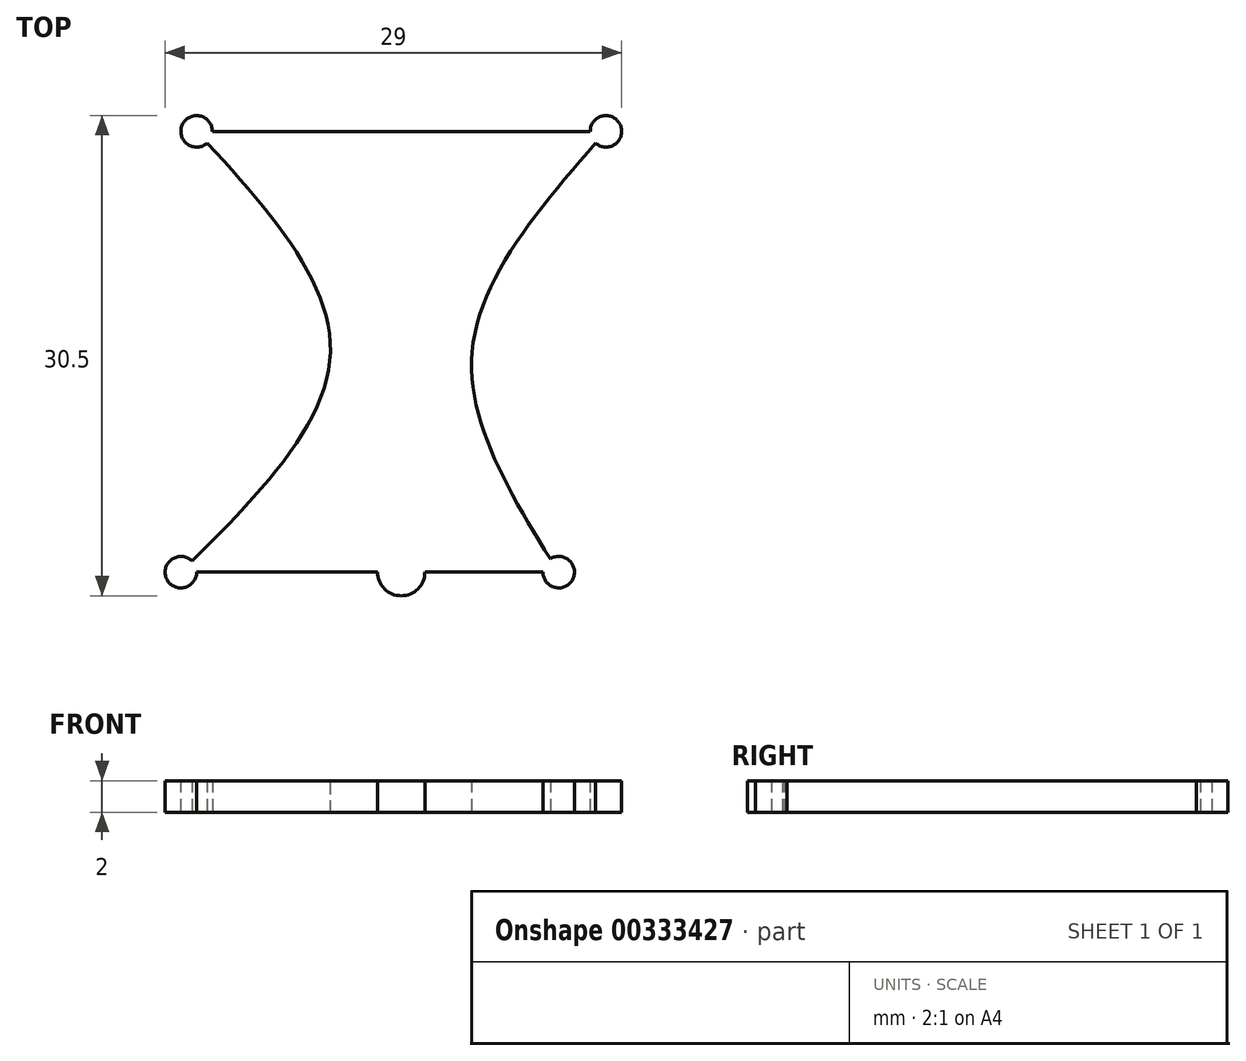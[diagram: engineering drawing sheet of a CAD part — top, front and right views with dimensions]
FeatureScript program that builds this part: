
annotation { "Feature Type Name" : "Feature", "Feature Type Description" : "" }
export const myFeature = defineFeature(function(context is Context, id is Id, definition is map)
    precondition{}
    {
        {
            var Q0;
            Q0=qCreatedBy(makeId("Top.planeOp"),FACE);
            var sketch = newSketch(context, id + "F0", { "sketchPlane" : qUnion([Q0])});
            skLineSegment(sketch, "E0", {"start": v(-13, 0) * mm, "end": v(13, 0) * mm});
            skArc(sketch, "E1", {"start": v(-1.5, 0) * mm, "mid": v(0, 1.5) * mm, "end": v(1.5, 0) * mm});
            skLineSegment(sketch, "E2", {"start": v(0, 0) * mm, "end": v(0, -28) * mm});
            skLineSegment(sketch, "E3", {"start": v(-14, -28) * mm, "end": v(10, -28) * mm});
            skPoint(sketch, "E4", {"position": v(0, -14) * mm});
            skLineSegment(sketch, "E5", {"start": v(-4.5, -14) * mm, "end": v(4.5, -14) * mm});
            skFitSpline(sketch, "E6", {"points": [v(-14, -28) * mm, v(-4.5, -14) * mm, v(-13, 0) * mm], "startDerivative": vector(27.92, 27.66) * mm, "endDerivative": vector(-26.06, 28.34) * mm});
            skFitSpline(sketch, "E7", {"points": [v(10, -28) * mm, v(4.5, -14) * mm, v(13, 0) * mm], "startDerivative": vector(-18.06, 28.9) * mm, "endDerivative": vector(23.77, 27.11) * mm});
            skCircle(sketch, "E8", {"center": v(13, 0) * mm, "radius": 1 * mm});
            skCircle(sketch, "E9", {"center": v(-13, 0) * mm, "radius": 1 * mm});
            skCircle(sketch, "E10", {"center": v(-14, -28) * mm, "radius": 1 * mm});
            skCircle(sketch, "E11", {"center": v(10, -28) * mm, "radius": 1 * mm});
            skArc(sketch, "E12", {"start": v(-1.5, -28) * mm, "mid": v(0, -29.5) * mm, "end": v(1.5, -28) * mm});
            skSolve(sketch);
        }
        {
            var Q0;
            {var subQ5=sQuery(id+"F0.wireOp",EDGE,"E0");var subQ7=makeQuery(id+"F0.imprint","INTERSECT",VERTEX,{"disambiguationData":[OD(0.0)],"derivedFrom":[subQ5,sQuery(id+"F0.wireOp",EDGE,"E1")]});Q0=makeQuery(id+"F0.imprint","IMPRINT",FACE,{"disambiguationData":[TD([[makeQuery(id+"F0.imprint","IMPRINT",EDGE,{"disambiguationData":[TD([[subQ7,1.0]])],"derivedFrom":subQ5}),-1.0]])]});}
            var Q1;
            {var subQ0=sQuery(id+"F0.wireOp",EDGE,"E6");var subQ1=sQuery(id+"F0.wireOp",EDGE,"E0");var subQ2=makeQuery(id+"F0.imprint","INTERSECT",VERTEX,{"derivedFrom":[subQ1,subQ0]});Q1=makeQuery(id+"F0.imprint","IMPRINT",FACE,{"disambiguationData":[TD([[makeQuery(id+"F0.imprint","IMPRINT",EDGE,{"disambiguationData":[TD([[subQ2,-1.0]])],"derivedFrom":subQ1}),1.0]])]});}
            var Q2;
            {var subQ0=sQuery(id+"F0.wireOp",EDGE,"E6");var subQ1=sQuery(id+"F0.wireOp",EDGE,"E0");var subQ2=makeQuery(id+"F0.imprint","INTERSECT",VERTEX,{"derivedFrom":[subQ1,subQ0]});Q2=makeQuery(id+"F0.imprint","IMPRINT",FACE,{"disambiguationData":[TD([[makeQuery(id+"F0.imprint","IMPRINT",EDGE,{"disambiguationData":[TD([[subQ2,-1.0]])],"derivedFrom":subQ1}),-1.0]])]});}
            var Q3;
            {var subQ0=sQuery(id+"F0.wireOp",EDGE,"E1");Q3=makeQuery(id+"F0.imprint","IMPRINT",FACE,{"disambiguationData":[TD([[makeQuery(id+"F0.imprint","IMPRINT",EDGE,{"derivedFrom":subQ0}),-1.0]])]});}
            var Q4;
            {var subQ5=sQuery(id+"F0.wireOp",EDGE,"E0");var subQ7=makeQuery(id+"F0.imprint","INTERSECT",VERTEX,{"disambiguationData":[OD(1.0)],"derivedFrom":[subQ5,sQuery(id+"F0.wireOp",EDGE,"E1")]});Q4=makeQuery(id+"F0.imprint","IMPRINT",FACE,{"disambiguationData":[TD([[makeQuery(id+"F0.imprint","IMPRINT",EDGE,{"disambiguationData":[TD([[subQ7,1.0]])],"derivedFrom":subQ5}),-1.0]])]});}
            var Q5;
            {var subQ0=sQuery(id+"F0.wireOp",EDGE,"E7");var subQ1=sQuery(id+"F0.wireOp",EDGE,"E0");var subQ2=makeQuery(id+"F0.imprint","INTERSECT",VERTEX,{"derivedFrom":[subQ1,subQ0]});Q5=makeQuery(id+"F0.imprint","IMPRINT",FACE,{"disambiguationData":[TD([[makeQuery(id+"F0.imprint","IMPRINT",EDGE,{"disambiguationData":[TD([[subQ2,1.0]])],"derivedFrom":subQ1}),-1.0]])]});}
            var Q6;
            {var subQ0=sQuery(id+"F0.wireOp",EDGE,"E7");var subQ1=sQuery(id+"F0.wireOp",EDGE,"E0");var subQ2=makeQuery(id+"F0.imprint","INTERSECT",VERTEX,{"derivedFrom":[subQ1,subQ0]});Q6=makeQuery(id+"F0.imprint","IMPRINT",FACE,{"disambiguationData":[TD([[makeQuery(id+"F0.imprint","IMPRINT",EDGE,{"disambiguationData":[TD([[subQ2,1.0]])],"derivedFrom":subQ1}),1.0]])]});}
            var Q7;
            {var subQ0=sQuery(id+"F0.wireOp",EDGE,"E7");var subQ1=sQuery(id+"F0.wireOp",EDGE,"E3");var subQ2=makeQuery(id+"F0.imprint","INTERSECT",VERTEX,{"derivedFrom":[subQ1,subQ0]});Q7=makeQuery(id+"F0.imprint","IMPRINT",FACE,{"disambiguationData":[TD([[makeQuery(id+"F0.imprint","IMPRINT",EDGE,{"disambiguationData":[TD([[subQ2,1.0]])],"derivedFrom":subQ1}),-1.0]])]});}
            var Q8;
            {var subQ0=sQuery(id+"F0.wireOp",EDGE,"E7");var subQ1=sQuery(id+"F0.wireOp",EDGE,"E3");var subQ2=makeQuery(id+"F0.imprint","INTERSECT",VERTEX,{"derivedFrom":[subQ1,subQ0]});Q8=makeQuery(id+"F0.imprint","IMPRINT",FACE,{"disambiguationData":[TD([[makeQuery(id+"F0.imprint","IMPRINT",EDGE,{"disambiguationData":[TD([[subQ2,1.0]])],"derivedFrom":subQ1}),1.0]])]});}
            var Q9;
            {var subQ3=sQuery(id+"F0.wireOp",EDGE,"E2");var subQ5=sQuery(id+"F0.wireOp",EDGE,"E3");var subQ6=makeQuery(id+"F0.imprint","INTERSECT",VERTEX,{"derivedFrom":[subQ3,subQ5]});Q9=makeQuery(id+"F0.imprint","IMPRINT",FACE,{"disambiguationData":[TD([[makeQuery(id+"F0.imprint","IMPRINT",EDGE,{"disambiguationData":[TD([[subQ6,1.0]])],"derivedFrom":subQ3}),1.0]])]});}
            var Q10;
            {var subQ2=sQuery(id+"F0.wireOp",EDGE,"E12");Q10=makeQuery(id+"F0.imprint","IMPRINT",FACE,{"disambiguationData":[TD([[makeQuery(id+"F0.imprint","IMPRINT",EDGE,{"derivedFrom":subQ2}),1.0]])]});}
            var Q11;
            {var subQ0=sQuery(id+"F0.wireOp",EDGE,"E3");var subQ1=sQuery(id+"F0.wireOp",EDGE,"E2");var subQ2=makeQuery(id+"F0.imprint","INTERSECT",VERTEX,{"derivedFrom":[subQ1,subQ0]});Q11=makeQuery(id+"F0.imprint","IMPRINT",FACE,{"disambiguationData":[TD([[makeQuery(id+"F0.imprint","IMPRINT",EDGE,{"disambiguationData":[TD([[subQ2,1.0]])],"derivedFrom":subQ1}),-1.0]])]});}
            var Q12;
            {var subQ0=sQuery(id+"F0.wireOp",EDGE,"E6");var subQ1=sQuery(id+"F0.wireOp",EDGE,"E3");var subQ2=makeQuery(id+"F0.imprint","INTERSECT",VERTEX,{"derivedFrom":[subQ1,subQ0]});Q12=makeQuery(id+"F0.imprint","IMPRINT",FACE,{"disambiguationData":[TD([[makeQuery(id+"F0.imprint","IMPRINT",EDGE,{"disambiguationData":[TD([[subQ2,-1.0]])],"derivedFrom":subQ1}),1.0]])]});}
            var Q13;
            {var subQ0=sQuery(id+"F0.wireOp",EDGE,"E6");var subQ1=sQuery(id+"F0.wireOp",EDGE,"E3");var subQ2=makeQuery(id+"F0.imprint","INTERSECT",VERTEX,{"derivedFrom":[subQ1,subQ0]});Q13=makeQuery(id+"F0.imprint","IMPRINT",FACE,{"disambiguationData":[TD([[makeQuery(id+"F0.imprint","IMPRINT",EDGE,{"disambiguationData":[TD([[subQ2,-1.0]])],"derivedFrom":subQ1}),-1.0]])]});}
            extrude(context, id + "F1", {"entities" : qUnion([Q0, Q1, Q2, Q3, Q4, Q5, Q6, Q7, Q8, Q9, Q10, Q11, Q12, Q13]), "depth" : 2 * mm});
        }
    });
